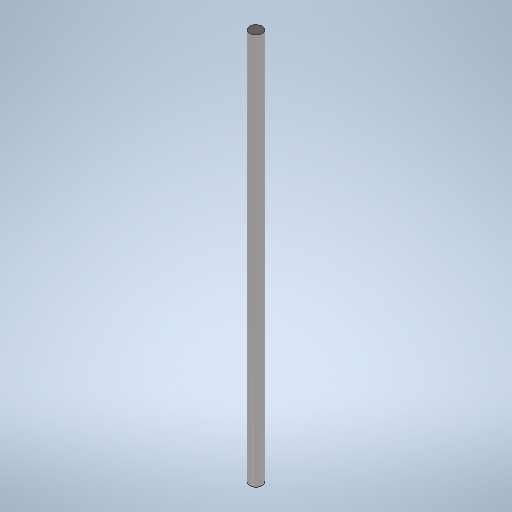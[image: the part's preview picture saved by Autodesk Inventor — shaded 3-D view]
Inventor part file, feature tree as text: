
AUTODESK INVENTOR PART (.ipt)
format: ipt  version: 2025.2 (Build 292293000, 293)  size: 235,520 bytes
history: native  units: mm
features: extrude x1, sketch x1
ambient origin geometry x8: Origin, YZ Plane, XZ Plane, XY Plane, X Axis, Y Axis, Z Axis, Center Point
bodies: Solid1 (feature_tree)
feature tree (2):
  extrude  "Extrusion1"  Depth=250.0mm TaperAngle=0.0deg
  sketch  "Sketch1"  dims[d0=8.0mm d1=250.0mm d2=0.0mm]
